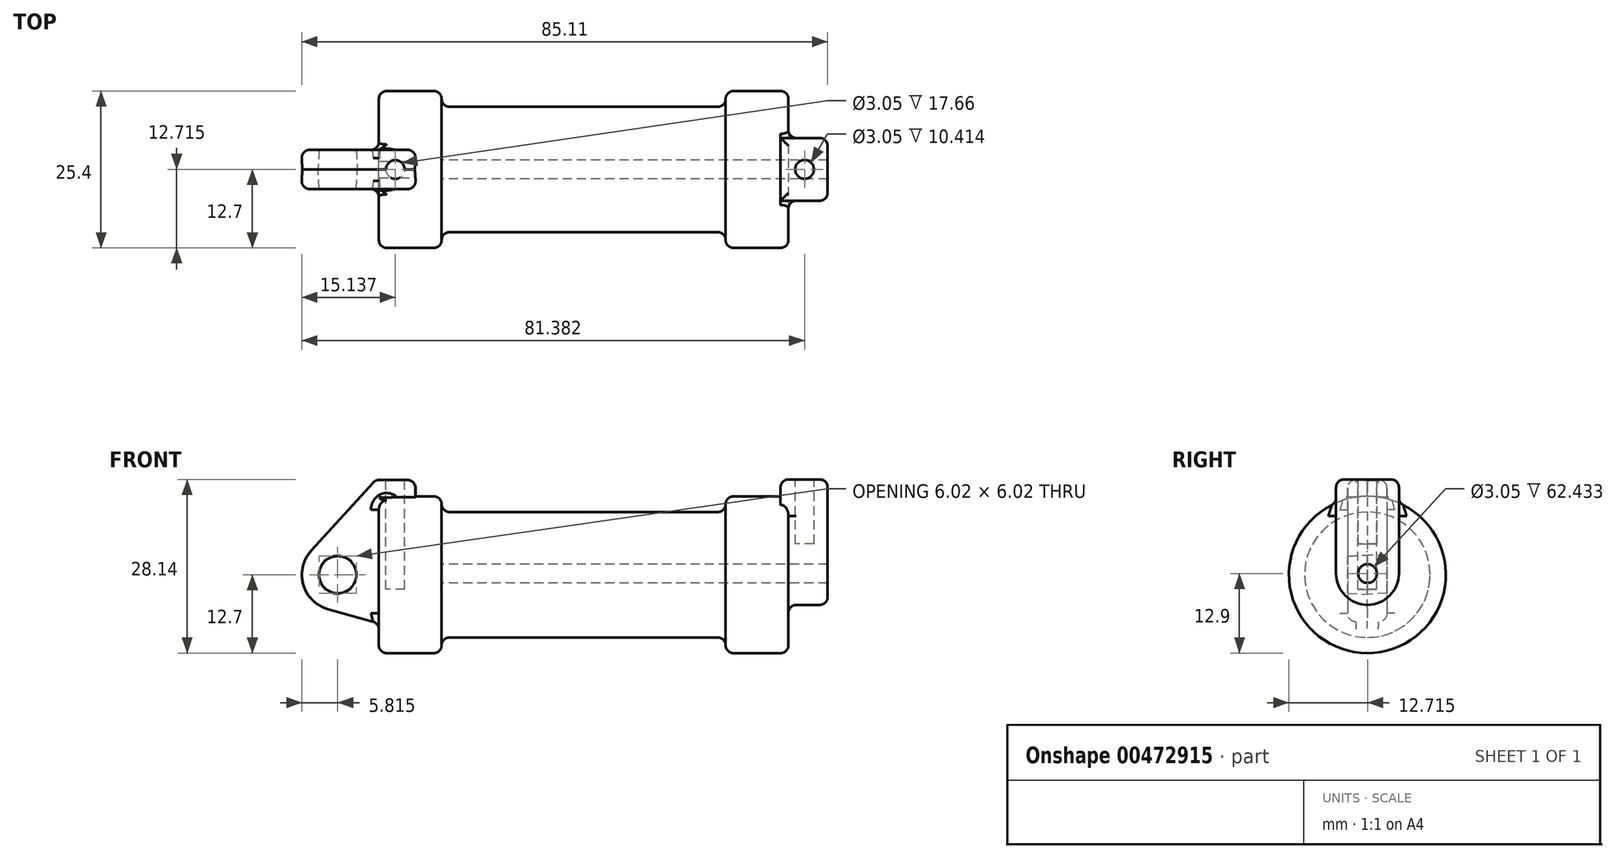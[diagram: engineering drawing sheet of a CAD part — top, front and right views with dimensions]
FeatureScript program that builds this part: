
annotation { "Feature Type Name" : "Feature", "Feature Type Description" : "" }
export const myFeature = defineFeature(function(context is Context, id is Id, definition is map)
    precondition{}
    {
        {
            var Q0;
            Q0=qCreatedBy(makeId("Front.planeOp"),FACE);
            var sketch = newSketch(context, id + "F0", { "sketchPlane" : qUnion([Q0])});
            skLineSegment(sketch, "E0", {"start": v(0, 0) * mm, "end": v(0, 12.7) * mm});
            skLineSegment(sketch, "E1", {"start": v(0, 12.7) * mm, "end": v(10.16, 12.7) * mm});
            skLineSegment(sketch, "E2", {"start": v(10.16, 12.7) * mm, "end": v(10.16, 10.16) * mm});
            skLineSegment(sketch, "E3", {"start": v(10.16, 10.16) * mm, "end": v(56.13, 10.16) * mm});
            skLineSegment(sketch, "E4", {"start": v(56.13, 10.16) * mm, "end": v(56.13, 12.7) * mm});
            skLineSegment(sketch, "E5", {"start": v(56.13, 12.7) * mm, "end": v(66.3, 12.7) * mm});
            skLineSegment(sketch, "E6", {"start": v(66.3, 12.7) * mm, "end": v(66.3, 0) * mm});
            skLineSegment(sketch, "E7", {"start": v(66.3, 0) * mm, "end": v(0, 0) * mm});
            skLineSegment(sketch, "E8", {"start": v(5.84, 15.24) * mm, "end": v(-0.5, 15.24) * mm});
            skLineSegment(sketch, "E9", {"start": v(-0.5, 15.24) * mm, "end": v(-10.88, 3.85) * mm});
            skLineSegment(sketch, "E10", {"start": v(0, 0) * mm, "end": v(-6.65, 0) * mm});
            skCircle(sketch, "E11", {"center": v(-6.65, 0) * mm, "radius": 5.72 * mm});
            skCircle(sketch, "E12", {"center": v(-6.65, 0) * mm, "radius": 3.18 * mm});
            skLineSegment(sketch, "E13", {"start": v(5.84, 15.24) * mm, "end": v(5.84, -9.4) * mm});
            skLineSegment(sketch, "E14", {"start": v(5.84, -9.4) * mm, "end": v(-8.18, -5.5) * mm});
            skSolve(sketch);
        }
        {
            var Q0;
            {var subQ0=sQuery(id+"F0.wireOp",EDGE,"E2");Q0=makeQuery(id+"F0.imprint","IMPRINT",FACE,{"disambiguationData":[TD([[makeQuery(id+"F0.imprint","IMPRINT",EDGE,{"derivedFrom":subQ0}),-1.0]])]});}
            var Q1;
            {var subQ0=sQuery(id+"F0.wireOp",EDGE,"E0");Q1=makeQuery(id+"F0.imprint","IMPRINT",FACE,{"disambiguationData":[TD([[makeQuery(id+"F0.imprint","IMPRINT",EDGE,{"derivedFrom":subQ0}),-1.0]])]});}
            var Q2;
            Q2=sQuery(id+"F0.wireOp",EDGE,"E7");
            revolve(context, id + "F1", {"entities" : qUnion([Q0, Q1]), "axis" : qUnion([Q2]), "revolveType" : RevolveType.FULL});
        }
        {
            var Q0;
            {var subQ1=sQuery(id+"F0.wireOp",EDGE,"E0");Q0=makeQuery(id+"F0.imprint","IMPRINT",FACE,{"disambiguationData":[TD([[makeQuery(id+"F0.imprint","IMPRINT",EDGE,{"derivedFrom":subQ1}),1.0]])]});}
            var Q1;
            {var subQ0=sQuery(id+"F0.wireOp",EDGE,"E14");Q1=makeQuery(id+"F0.imprint","IMPRINT",FACE,{"disambiguationData":[TD([[makeQuery(id+"F0.imprint","IMPRINT",EDGE,{"derivedFrom":subQ0}),-1.0]])]});}
            var Q2;
            {var subQ5=sQuery(id+"F0.wireOp",EDGE,"E12");Q2=makeQuery(id+"F0.imprint","IMPRINT",FACE,{"disambiguationData":[TD([[makeQuery(id+"F0.imprint","IMPRINT",EDGE,{"derivedFrom":subQ5}),-1.0]])]});}
            extrude(context, id + "F2", {"entities" : qUnion([Q0, Q1, Q2]), "operationType" : NewBodyOperationType.ADD, "endBound" : BoundingType.SYMMETRIC, "oppositeDirection" : true, "depth" : 6.35 * mm, "hasDraft" : true, "draftAngle" : 3 * degree});
        }
        {
            var Q0;
            Q0=makeQuery(id+"F1.opRevolve","SWEPT_FACE",FACE,{"disambiguationData":[OSD([sQuery(id+"F0.wireOp",EDGE,"E6")])]});
            var sketch = newSketch(context, id + "F3", { "sketchPlane" : qUnion([Q0])});
            skSolve(sketch);
        }
        {
            var Q0;
            Q0=makeQuery(id+"F3.imprint","IMPRINT",FACE,{"disambiguationData":[TD([[makeQuery(id+"F3.imprint","IMPRINT",EDGE,{"derivedFrom":makeQuery(id+"F1.opRevolve","SWEPT_EDGE",EDGE,{"disambiguationData":[OSD([sQuery(id+"F0.wireOp",EDGE,"E5"),sQuery(id+"F0.wireOp",EDGE,"E6")])]})}),1.0]])]});
            var sketch = newSketch(context, id + "F4", { "sketchPlane" : qUnion([Q0])});
            skCircle(sketch, "E15", {"center": v(0.01, 0.2) * mm, "radius": 1.52 * mm});
            skCircle(sketch, "E16", {"center": v(0.01, 0.2) * mm, "radius": 5.08 * mm});
            skLineSegment(sketch, "E17", {"start": v(-5.07, 15.44) * mm, "end": v(-5.07, 0.2) * mm});
            skLineSegment(sketch, "E18", {"start": v(5.1, 15.44) * mm, "end": v(5.1, 0.2) * mm});
            skLineSegment(sketch, "E19", {"start": v(-5.07, 15.44) * mm, "end": v(5.1, 15.44) * mm});
            skSolve(sketch);
        }
        {
            var Q0;
            Q0 = qSketchRegion(id + "F4", true);
            extrude(context, id + "F5", {"entities" : qUnion([Q0]), "operationType" : NewBodyOperationType.ADD, "depth" : 6.35 * mm});
        }
        {
            var Q0;
            Q0=makeQuery(id+"F5.opExtrude","CAP_FACE",FACE,{"disambiguationData":[OSD([sQuery(id+"F4.wireOp",EDGE,"E15"),sQuery(id+"F4.wireOp",EDGE,"E16"),sQuery(id+"F4.wireOp",EDGE,"E17"),sQuery(id+"F4.wireOp",EDGE,"E18"),sQuery(id+"F4.wireOp",EDGE,"E19")])],"isStart":true});
            extrude(context, id + "F6", {"entities" : qUnion([Q0]), "operationType" : NewBodyOperationType.ADD, "depth" : 1.27 * mm});
        }
        {
            var Q0;
            Q0=makeQuery(id+"F4.imprint","IMPRINT",FACE,{"disambiguationData":[TD([[makeQuery(id+"F4.imprint","IMPRINT",EDGE,{"derivedFrom":sQuery(id+"F4.wireOp",EDGE,"E15")}),1.0]])]});
            extrude(context, id + "F7", {"entities" : qUnion([Q0]), "operationType" : NewBodyOperationType.REMOVE, "oppositeDirection" : true, "depth" : 56.08 * mm});
        }
        {
            var Q0;
            {var subQ0=sQuery(id+"F4.wireOp",EDGE,"E19");Q0=makeQuery(id+"F6.boolean.opBoolean","MERGE",FACE,{"derivedFrom":[makeQuery(id+"F5.opExtrude","SWEPT_FACE",FACE,{"disambiguationData":[OSD([subQ0])]}),makeQuery(id+"F6.opExtrude","SWEPT_FACE",FACE,{"disambiguationData":[OSD([subQ0])]})]});}
            var sketch = newSketch(context, id + "F8", { "sketchPlane" : qUnion([Q0])});
            skCircle(sketch, "E20", {"center": v(68.91, 0.01) * mm, "radius": 1.52 * mm});
            skCircle(sketch, "E21", {"center": v(2.67, 0) * mm, "radius": 1.52 * mm});
            skLineSegment(sketch, "E22", {"start": v(65.18, 0.01) * mm, "end": v(72.64, 0.01) * mm});
            skPoint(sketch, "E22.startSnap0", {"position": v(65.02, 0.01) * mm});
            skSolve(sketch);
        }
        {
            var Q0;
            Q0=makeQuery(id+"F8.imprint","IMPRINT",FACE,{"disambiguationData":[TD([[makeQuery(id+"F8.imprint","IMPRINT",EDGE,{"derivedFrom":sQuery(id+"F8.wireOp",EDGE,"E21")}),1.0]])]});
            extrude(context, id + "F9", {"entities" : qUnion([Q0]), "operationType" : NewBodyOperationType.REMOVE, "oppositeDirection" : true, "depth" : 17.78 * mm});
        }
        {
            var Q0;
            {var subQ0=sQuery(id+"F8.wireOp",EDGE,"E22");var subQ1=sQuery(id+"F8.wireOp",EDGE,"E20");var subQ2=makeQuery(id+"F8.imprint","INTERSECT",VERTEX,{"disambiguationData":[OD(0.0)],"derivedFrom":[subQ1,subQ0]});Q0=makeQuery(id+"F8.imprint","IMPRINT",FACE,{"disambiguationData":[TD([[makeQuery(id+"F8.imprint","IMPRINT",EDGE,{"disambiguationData":[TD([[subQ2,-1.0]])],"derivedFrom":subQ1}),1.0]])]});}
            var Q1;
            {var subQ0=sQuery(id+"F8.wireOp",EDGE,"E22");var subQ1=sQuery(id+"F8.wireOp",EDGE,"E20");var subQ2=makeQuery(id+"F8.imprint","INTERSECT",VERTEX,{"disambiguationData":[OD(0.0)],"derivedFrom":[subQ1,subQ0]});Q1=makeQuery(id+"F8.imprint","IMPRINT",FACE,{"disambiguationData":[TD([[makeQuery(id+"F8.imprint","IMPRINT",EDGE,{"disambiguationData":[TD([[subQ2,1.0]])],"derivedFrom":subQ1}),1.0]])]});}
            extrude(context, id + "F10", {"entities" : qUnion([Q0, Q1]), "operationType" : NewBodyOperationType.REMOVE, "oppositeDirection" : true, "depth" : 10.4 * mm});
        }
        {
            var Q0;
            Q0=makeQuery(id+"F5.boolean.opBoolean","SPLIT",FACE,{"disambiguationData":[TD([makeQuery(id+"F1.opRevolve","SWEPT_FACE",FACE,{"disambiguationData":[OSD([sQuery(id+"F0.wireOp",EDGE,"E5")])]})])],"derivedFrom":makeQuery(id+"F1.opRevolve","SWEPT_FACE",FACE,{"disambiguationData":[OSD([sQuery(id+"F0.wireOp",EDGE,"E6")])]})});
            var Q1;
            Q1=makeQuery(id+"F5.opExtrude","CAP_EDGE",EDGE,{"disambiguationData":[OSD([sQuery(id+"F4.wireOp",EDGE,"E16")])],"isStart":false});
            var Q2;
            Q2=makeQuery(id+"F5.opExtrude","CAP_EDGE",EDGE,{"disambiguationData":[OSD([sQuery(id+"F4.wireOp",EDGE,"E19")])],"isStart":false});
            var Q3;
            {var subQ0=sQuery(id+"F4.wireOp",EDGE,"E19");var subQ1=sQuery(id+"F4.wireOp",EDGE,"E18");Q3=makeQuery(id+"F6.boolean.opBoolean","MERGE",EDGE,{"derivedFrom":[makeQuery(id+"F5.opExtrude","SWEPT_EDGE",EDGE,{"disambiguationData":[OSD([subQ1,subQ0])]}),makeQuery(id+"F6.opExtrude","SWEPT_EDGE",EDGE,{"disambiguationData":[OSD([subQ1,subQ0])]})]});}
            var Q4;
            {var subQ0=sQuery(id+"F4.wireOp",EDGE,"E19");var subQ1=sQuery(id+"F4.wireOp",EDGE,"E17");Q4=makeQuery(id+"F6.boolean.opBoolean","MERGE",EDGE,{"derivedFrom":[makeQuery(id+"F5.opExtrude","SWEPT_EDGE",EDGE,{"disambiguationData":[OSD([subQ1,subQ0])]}),makeQuery(id+"F6.opExtrude","SWEPT_EDGE",EDGE,{"disambiguationData":[OSD([subQ1,subQ0])]})]});}
            var Q5;
            Q5=makeQuery(id+"F6.opExtrude","CAP_EDGE",EDGE,{"disambiguationData":[OSD([sQuery(id+"F4.wireOp",EDGE,"E19")])],"isStart":false});
            var Q6;
            Q6=makeQuery(id+"F1.opRevolve","SWEPT_EDGE",EDGE,{"disambiguationData":[OSD([sQuery(id+"F0.wireOp",EDGE,"E4"),sQuery(id+"F0.wireOp",EDGE,"E5")])]});
            var Q7;
            Q7=makeQuery(id+"F1.opRevolve","SWEPT_EDGE",EDGE,{"disambiguationData":[OSD([sQuery(id+"F0.wireOp",EDGE,"E1"),sQuery(id+"F0.wireOp",EDGE,"E2")])]});
            var Q8;
            Q8=makeQuery(id+"F1.opRevolve","SWEPT_EDGE",EDGE,{"disambiguationData":[OSD([sQuery(id+"F0.wireOp",EDGE,"E0"),sQuery(id+"F0.wireOp",EDGE,"E1")])]});
            var Q9;
            Q9=makeQuery(id+"F2.opExtrude","CAP_EDGE",EDGE,{"disambiguationData":[OSD([sQuery(id+"F0.wireOp",EDGE,"E14")])],"isStart":true});
            var Q10;
            Q10=makeQuery(id+"F2.opExtrude","CAP_EDGE",EDGE,{"disambiguationData":[OSD([sQuery(id+"F0.wireOp",EDGE,"E8")])],"isStart":true});
            var Q11;
            Q11=makeQuery(id+"F2.opExtrude","CAP_EDGE",EDGE,{"disambiguationData":[OSD([sQuery(id+"F0.wireOp",EDGE,"E11")])],"isStart":false});
            var Q12;
            Q12=makeQuery(id+"F2.opExtrude","CAP_EDGE",EDGE,{"disambiguationData":[OSD([sQuery(id+"F0.wireOp",EDGE,"E8")])],"isStart":false});
            var Q13;
            Q13=makeQuery(id+"F2.*.split.splitOp","SPLIT",EDGE,{"derivedFrom":makeQuery(id+"F2.opExtrude","SWEPT_EDGE",EDGE,{"disambiguationData":[OSD([sQuery(id+"F0.wireOp",EDGE,"E8"),sQuery(id+"F0.wireOp",EDGE,"E9")])]}),"isFromBackBody":true});
            var Q14;
            Q14=makeQuery(id+"F2.*.split.splitOp","SPLIT",EDGE,{"derivedFrom":makeQuery(id+"F2.opExtrude","SWEPT_EDGE",EDGE,{"disambiguationData":[OSD([sQuery(id+"F0.wireOp",EDGE,"E8"),sQuery(id+"F0.wireOp",EDGE,"E9")])]})});
            var Q15;
            Q15=makeQuery(id+"F2.*.split.splitOp","SPLIT",EDGE,{"derivedFrom":makeQuery(id+"F2.opExtrude","SWEPT_EDGE",EDGE,{"disambiguationData":[OSD([sQuery(id+"F0.wireOp",EDGE,"E8"),sQuery(id+"F0.wireOp",EDGE,"E13")])]}),"isFromBackBody":true});
            var Q16;
            Q16=makeQuery(id+"F2.*.split.splitOp","SPLIT",EDGE,{"derivedFrom":makeQuery(id+"F2.opExtrude","SWEPT_EDGE",EDGE,{"disambiguationData":[OSD([sQuery(id+"F0.wireOp",EDGE,"E8"),sQuery(id+"F0.wireOp",EDGE,"E13")])]})});
            var Q17;
            Q17=makeQuery(id+"F1.opRevolve","SWEPT_EDGE",EDGE,{"disambiguationData":[OSD([sQuery(id+"F0.wireOp",EDGE,"E2"),sQuery(id+"F0.wireOp",EDGE,"E3")])]});
            var Q18;
            {var subQ0=sQuery(id+"F0.wireOp",EDGE,"E13");Q18=makeQuery(id+"F2.opExtrude","CAP_EDGE",EDGE,{"disambiguationData":[OSD([subQ0]),TDD([makeQuery(id+"F0.imprint","IMPRINT",EDGE,{"disambiguationData":[TD([[makeQuery(id+"F0.imprint","INTERSECT",VERTEX,{"derivedFrom":[sQuery(id+"F0.wireOp",EDGE,"E8"),subQ0]}),-1.0]])],"derivedFrom":subQ0})])],"isStart":false});}
            var Q19;
            {var subQ0=sQuery(id+"F0.wireOp",EDGE,"E13");Q19=makeQuery(id+"F2.opExtrude","CAP_EDGE",EDGE,{"disambiguationData":[OSD([subQ0]),TDD([makeQuery(id+"F0.imprint","IMPRINT",EDGE,{"disambiguationData":[TD([[makeQuery(id+"F0.imprint","INTERSECT",VERTEX,{"derivedFrom":[sQuery(id+"F0.wireOp",EDGE,"E8"),subQ0]}),-1.0]])],"derivedFrom":subQ0})])],"isStart":true});}
            fillet(context, id + "F11", {"entities" : qUnion([Q0, Q1, Q2, Q3, Q4, Q5, Q6, Q7, Q8, Q9, Q10, Q11, Q12, Q13, Q14, Q15, Q16, Q17, Q18, Q19]), "radius" : 1.27 * mm, "tangentPropagation" : true, "allowEdgeOverflow" : false});
        }
        {
            var Q0;
            Q0=makeQuery(id+"F1.opRevolve","SWEPT_EDGE",EDGE,{"disambiguationData":[OSD([sQuery(id+"F0.wireOp",EDGE,"E3"),sQuery(id+"F0.wireOp",EDGE,"E4")])]});
            var Q1;
            {var subQ0=sQuery(id+"F0.wireOp",EDGE,"E0");Q1=makeQuery(id+"F2.boolean.opBoolean","INTERSECT",EDGE,{"derivedFrom":[makeQuery(id+"F1.opRevolve","SWEPT_FACE",FACE,{"disambiguationData":[OSD([subQ0])]}),makeQuery(id+"F2.opExtrude","CAP_FACE",FACE,{"disambiguationData":[OSD([subQ0,sQuery(id+"F0.wireOp",EDGE,"E1"),sQuery(id+"F0.wireOp",EDGE,"E7"),sQuery(id+"F0.wireOp",EDGE,"E8"),sQuery(id+"F0.wireOp",EDGE,"E9"),sQuery(id+"F0.wireOp",EDGE,"E11"),sQuery(id+"F0.wireOp",EDGE,"E12"),sQuery(id+"F0.wireOp",EDGE,"E13"),sQuery(id+"F0.wireOp",EDGE,"E14")])],"isStart":true})]});}
            var Q2;
            Q2=makeQuery(id+"F11.opFillet","BLEND_EDGE",EDGE,{"blendedFrom":[makeQuery(id+"F2.opExtrude","CAP_EDGE",EDGE,{"disambiguationData":[OSD([sQuery(id+"F0.wireOp",EDGE,"E14")])],"isStart":true}),makeQuery(id+"F1.opRevolve","SWEPT_FACE",FACE,{"disambiguationData":[OSD([sQuery(id+"F0.wireOp",EDGE,"E0")])]})],"blendedInto":[makeQuery(id+"F1.opRevolve","SWEPT_FACE",FACE,{"disambiguationData":[OSD([sQuery(id+"F0.wireOp",EDGE,"E0")])]})]});
            var Q3;
            Q3=makeQuery(id+"F2.boolean.opBoolean","INTERSECT",EDGE,{"derivedFrom":[makeQuery(id+"F1.opRevolve","SWEPT_FACE",FACE,{"disambiguationData":[OSD([sQuery(id+"F0.wireOp",EDGE,"E0")])]}),makeQuery(id+"F2.*.split.splitOp","SPLIT",FACE,{"derivedFrom":makeQuery(id+"F2.opExtrude","SWEPT_FACE",FACE,{"disambiguationData":[OSD([sQuery(id+"F0.wireOp",EDGE,"E14")])]})})]});
            fillet(context, id + "F12", {"entities" : qUnion([Q0, Q1, Q2, Q3]), "radius" : 1.27 * mm, "tangentPropagation" : true, "allowEdgeOverflow" : false});
        }
    });
